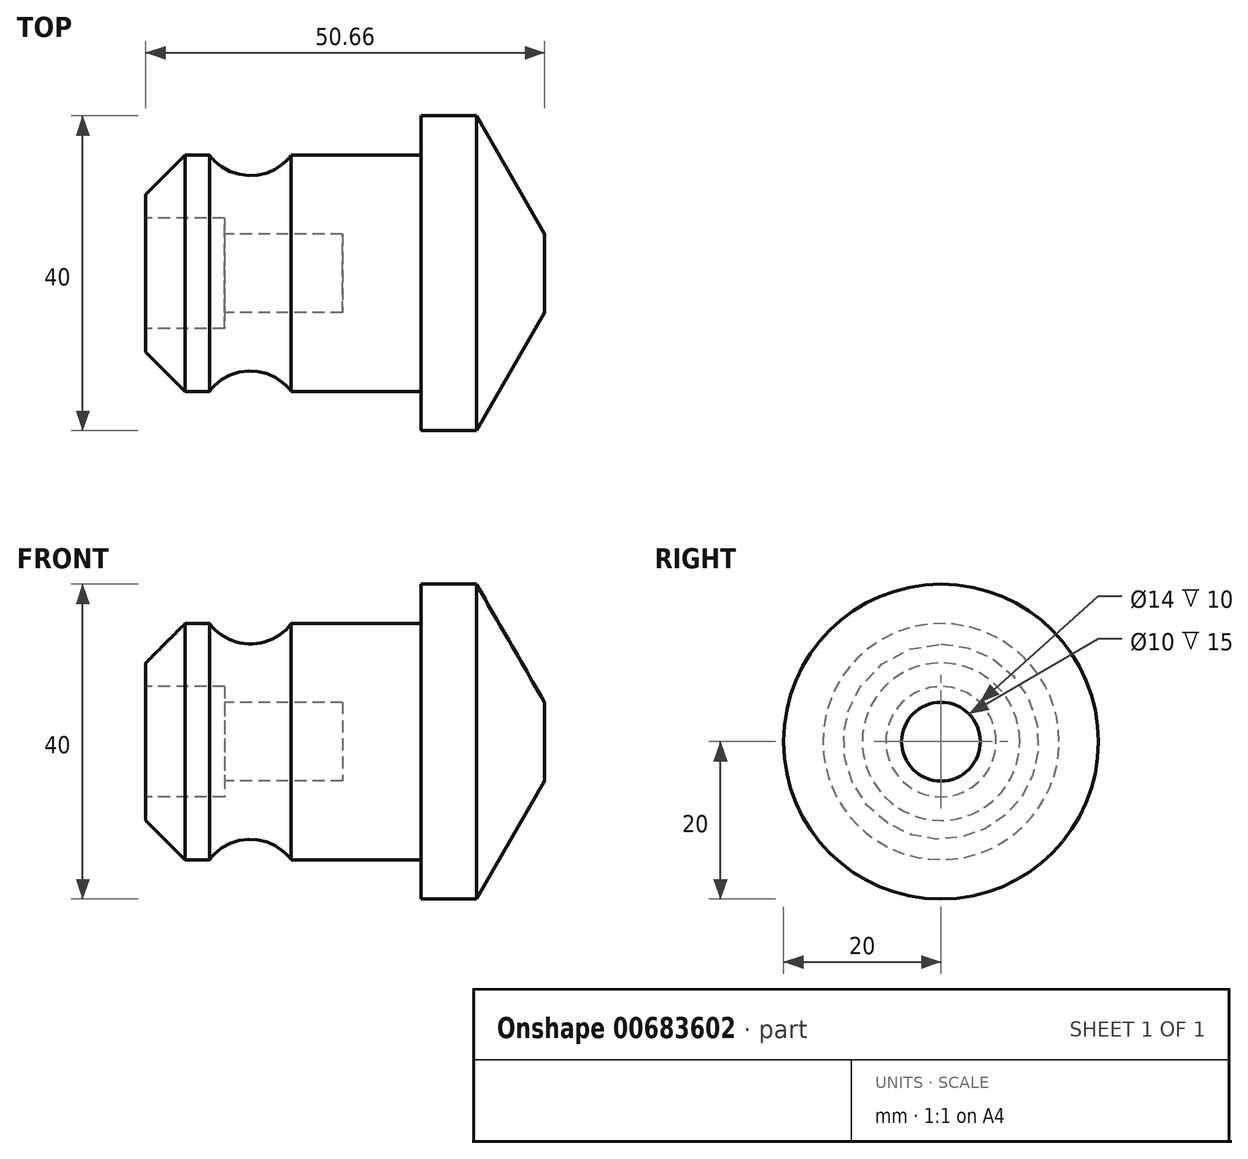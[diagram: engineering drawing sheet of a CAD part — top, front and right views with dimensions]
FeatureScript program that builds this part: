
annotation { "Feature Type Name" : "Feature", "Feature Type Description" : "" }
export const myFeature = defineFeature(function(context is Context, id is Id, definition is map)
    precondition{}
    {
        {
            var Q0;
            Q0=qCreatedBy(makeId("Front.planeOp"),FACE);
            var sketch = newSketch(context, id + "F0", { "sketchPlane" : qUnion([Q0])});
            skLineSegment(sketch, "E0", {"start": v(-1, 0) * mm, "end": v(-1, 5) * mm});
            skLineSegment(sketch, "E1", {"start": v(-1, 5) * mm, "end": v(-9.66, 20) * mm});
            skLineSegment(sketch, "E2", {"start": v(-9.66, 20) * mm, "end": v(-16.66, 20) * mm});
            skLineSegment(sketch, "E3", {"start": v(-16.66, 20) * mm, "end": v(-16.66, 15) * mm});
            skLineSegment(sketch, "E4", {"start": v(-16.66, 15) * mm, "end": v(-46.66, 15) * mm});
            skLineSegment(sketch, "E5", {"start": v(-46.66, 15) * mm, "end": v(-51.66, 10) * mm});
            skLineSegment(sketch, "E6", {"start": v(-51.66, 10) * mm, "end": v(-51.66, 7) * mm});
            skLineSegment(sketch, "E7", {"start": v(-51.66, 7) * mm, "end": v(-41.66, 7) * mm});
            skLineSegment(sketch, "E8", {"start": v(-41.66, 7) * mm, "end": v(-41.66, 5) * mm});
            skLineSegment(sketch, "E9", {"start": v(-41.66, 5) * mm, "end": v(-26.66, 5) * mm});
            skLineSegment(sketch, "E10", {"start": v(-26.66, 5) * mm, "end": v(-26.66, 0) * mm});
            skLineSegment(sketch, "E11", {"start": v(-26.66, 0) * mm, "end": v(-1, 0) * mm});
            skLineSegment(sketch, "E12", {"start": v(-68.54, 0) * mm, "end": v(7.8, 0) * mm, "construction": true});
            skCircle(sketch, "E13", {"center": v(-38.36, 18.9) * mm, "radius": 6.5 * mm});
            skSolve(sketch);
        }
        {
            var Q0;
            Q0=makeQuery(id+"F0.imprint","IMPRINT",FACE,{"disambiguationData":[TD([[makeQuery(id+"F0.imprint","IMPRINT",EDGE,{"derivedFrom":sQuery(id+"F0.wireOp",EDGE,"E0")}),1.0]])]});
            var Q1;
            Q1=sQuery(id+"F0.wireOp",EDGE,"E12");
            revolve(context, id + "F1", {"surfaceOperationType" : NewSurfaceOperationType.NEW, "entities" : qUnion([Q0]), "axis" : qUnion([Q1]), "revolveType" : RevolveType.FULL});
        }
    });
